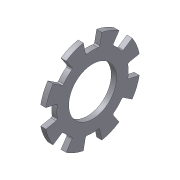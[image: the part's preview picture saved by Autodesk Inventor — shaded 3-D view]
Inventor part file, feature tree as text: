
AUTODESK INVENTOR PART (.ipt)
format: ipt  version: 2015 SP1 (Build 190203100, 203)  size: 133,632 bytes
history: native  units: mm (DEFAULTED — no unit token found)
features: sketch x2, extrude x1, pattern_circular x1
ambient origin geometry x8: Origin, YZ Plane, XZ Plane, XY Plane, X Axis, Y Axis, Z Axis, Center Point
bodies: Solid1 (feature_tree), Body (feature_tree)
feature tree (4):
  extrude  "Cut"  Depth=6.5024mm
  pattern_circular  "Cuts"  [2 undecoded]
  sketch  "Sketch1"  dims[d0=12.954mm d1=6.5024mm]
  sketch  "Sketch2"  dims[d2=0.7112mm d3=0.0mm d4=22.5deg d5=9.7282mm d6=0.7112mm d7=0.0mm d8=0.19431mm d9=80.0mm d11=360.0deg d12=0.0mm d13=0.0mm]
note: 2 required parameter values undecoded (feature->parameter linkage not recoverable at this tier; creation-order binding heuristic only, values carry confidence <= 0.55)
